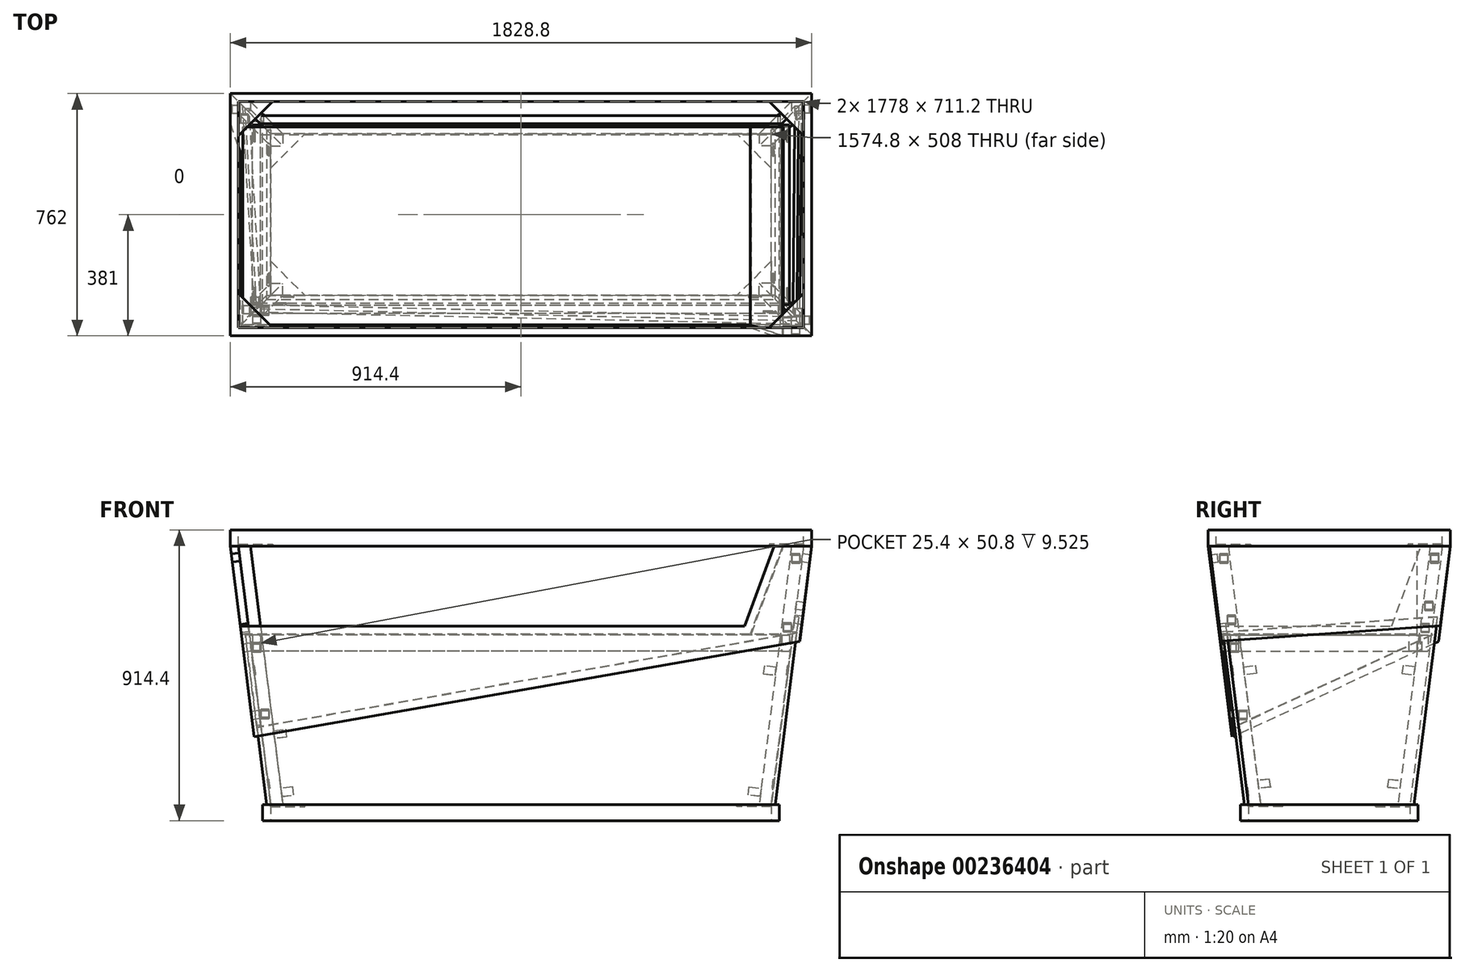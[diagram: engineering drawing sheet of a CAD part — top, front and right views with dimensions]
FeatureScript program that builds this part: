
annotation { "Feature Type Name" : "Feature", "Feature Type Description" : "" }
export const myFeature = defineFeature(function(context is Context, id is Id, definition is map)
    precondition{}
    {
        {
            var Q0;
            Q0=qCreatedBy(makeId("Top.planeOp"),FACE);
            cPlane(context, id + "F0", {"entities" : qUnion([Q0]), "cplaneType" : CPlaneType.OFFSET, "offset" : 914.4 * mm, "width" : 152.4 * mm, "height" : 152.4 * mm});
        }
        {
            var Q0;
            Q0=qCreatedBy(id+"F0.planeOp",FACE);
            var sketch = newSketch(context, id + "F1", { "sketchPlane" : qUnion([Q0])});
            skLineSegment(sketch, "E0.bottom", {"start": v(914.4, -381) * mm, "end": v(-914.4, -381) * mm});
            skLineSegment(sketch, "E0.top", {"start": v(914.4, 381) * mm, "end": v(-914.4, 381) * mm});
            skLineSegment(sketch, "E0.left", {"start": v(914.4, -381) * mm, "end": v(914.4, 381) * mm});
            skLineSegment(sketch, "E0.right", {"start": v(-914.4, -381) * mm, "end": v(-914.4, 381) * mm});
            skPoint(sketch, "E0.middle", {"position": v(0, 0) * mm});
            skLineSegment(sketch, "E1.0", {"start": v(889, 355.6) * mm, "end": v(-889, 355.6) * mm});
            skLineSegment(sketch, "E1.1", {"start": v(889, -355.6) * mm, "end": v(889, 355.6) * mm});
            skLineSegment(sketch, "E1.2", {"start": v(889, -355.6) * mm, "end": v(-889, -355.6) * mm});
            skLineSegment(sketch, "E1.3", {"start": v(-889, -355.6) * mm, "end": v(-889, 355.6) * mm});
            skSolve(sketch);
        }
        {
            var Q0;
            Q0 = qSketchRegion(id + "F1", true);
            extrude(context, id + "F2", {"entities" : qUnion([Q0]), "oppositeDirection" : true, "depth" : 50.8 * mm});
        }
        {
            var Q0;
            Q0=qCreatedBy(makeId("Top.planeOp"),FACE);
            var sketch = newSketch(context, id + "F3", { "sketchPlane" : qUnion([Q0])});
            skLineSegment(sketch, "E2.bottom", {"start": v(812.8, -279.4) * mm, "end": v(-812.8, -279.4) * mm});
            skLineSegment(sketch, "E2.top", {"start": v(812.8, 279.4) * mm, "end": v(-812.8, 279.4) * mm});
            skLineSegment(sketch, "E2.left", {"start": v(812.8, -279.4) * mm, "end": v(812.8, 279.4) * mm});
            skLineSegment(sketch, "E2.right", {"start": v(-812.8, -279.4) * mm, "end": v(-812.8, 279.4) * mm});
            skPoint(sketch, "E2.middle", {"position": v(0, 0) * mm});
            skLineSegment(sketch, "E3.0", {"start": v(787.4, 254) * mm, "end": v(-787.4, 254) * mm});
            skLineSegment(sketch, "E3.1", {"start": v(787.4, -254) * mm, "end": v(787.4, 254) * mm});
            skLineSegment(sketch, "E3.2", {"start": v(787.4, -254) * mm, "end": v(-787.4, -254) * mm});
            skLineSegment(sketch, "E3.3", {"start": v(-787.4, -254) * mm, "end": v(-787.4, 254) * mm});
            skSolve(sketch);
        }
        {
            var Q0;
            Q0 = qSketchRegion(id + "F3", true);
            extrude(context, id + "F4", {"entities" : qUnion([Q0]), "depth" : 50.8 * mm});
        }
        {
            var Q0;
            Q0=makeQuery(id+"F4.opExtrude","CAP_FACE",FACE,{"disambiguationData":[OSD([sQuery(id+"F3.wireOp",EDGE,"E2.bottom"),sQuery(id+"F3.wireOp",EDGE,"E2.top"),sQuery(id+"F3.wireOp",EDGE,"E2.left"),sQuery(id+"F3.wireOp",EDGE,"E2.right"),sQuery(id+"F3.wireOp",EDGE,"E3.0"),sQuery(id+"F3.wireOp",EDGE,"E3.1"),sQuery(id+"F3.wireOp",EDGE,"E3.2"),sQuery(id+"F3.wireOp",EDGE,"E3.3")])],"isStart":true});
            var sketch = newSketch(context, id + "F5", { "sketchPlane" : qUnion([Q0])});
            skLineSegment(sketch, "E4", {"start": v(-787.4, 496.92) * mm, "end": v(-787.4, -532.99) * mm, "construction": true});
            skLineSegment(sketch, "E5.MirrorCS", {"start": v(787.4, 496.92) * mm, "end": v(787.4, -532.99) * mm, "construction": true});
            skSolve(sketch);
        }
        {
            var Q0;
            Q0=makeQuery(id+"F2.opExtrude","CAP_FACE",FACE,{"disambiguationData":[OSD([sQuery(id+"F1.wireOp",EDGE,"E0.bottom"),sQuery(id+"F1.wireOp",EDGE,"E0.top"),sQuery(id+"F1.wireOp",EDGE,"E0.left"),sQuery(id+"F1.wireOp",EDGE,"E0.right"),sQuery(id+"F1.wireOp",EDGE,"E1.0"),sQuery(id+"F1.wireOp",EDGE,"E1.1"),sQuery(id+"F1.wireOp",EDGE,"E1.2"),sQuery(id+"F1.wireOp",EDGE,"E1.3")])],"isStart":false});
            var sketch = newSketch(context, id + "F6", { "sketchPlane" : qUnion([Q0])});
            skLineSegment(sketch, "E6", {"start": v(-889, 355.6) * mm, "end": v(-889, 247.84) * mm});
            skLineSegment(sketch, "E7", {"start": v(-889, 247.84) * mm, "end": v(-781.24, 355.6) * mm});
            skLineSegment(sketch, "E8", {"start": v(-781.24, 355.6) * mm, "end": v(-889, 355.6) * mm});
            skSolve(sketch);
        }
        {
            var Q0;
            Q0 = qSketchRegion(id + "F6", true);
            extrude(context, id + "F7", {"entities" : qUnion([Q0]), "oppositeDirection" : true, "depth" : 6.35 * mm});
        }
        {
            var Q0;
            Q0=makeQuery(id+"F7.opExtrude","SWEPT_BODY",BODY,{"disambiguationData":[OSD([sQuery(id+"F6.wireOp",EDGE,"E6"),sQuery(id+"F6.wireOp",EDGE,"E7"),sQuery(id+"F6.wireOp",EDGE,"E8")])]});
            var Q1;
            Q1=qCreatedBy(makeId("Front.planeOp"),FACE);
            mirror(context, id + "F8", {"entities" : qUnion([Q0]), "mirrorPlane" : qUnion([Q1])});
        }
        {
            var Q0;
            Q0=makeQuery(id+"F8.opPattern","COPY",BODY,{"derivedFrom":makeQuery(id+"F7.opExtrude","SWEPT_BODY",BODY,{"disambiguationData":[OSD([sQuery(id+"F6.wireOp",EDGE,"E6"),sQuery(id+"F6.wireOp",EDGE,"E7"),sQuery(id+"F6.wireOp",EDGE,"E8")])]}),"instanceName":"1"});
            var Q1;
            Q1=makeQuery(id+"F7.opExtrude","SWEPT_BODY",BODY,{"disambiguationData":[OSD([sQuery(id+"F6.wireOp",EDGE,"E6"),sQuery(id+"F6.wireOp",EDGE,"E7"),sQuery(id+"F6.wireOp",EDGE,"E8")])]});
            var Q2;
            Q2=qCreatedBy(makeId("Right.planeOp"),FACE);
            mirror(context, id + "F9", {"entities" : qUnion([Q0, Q1]), "mirrorPlane" : qUnion([Q2])});
        }
        {
            var Q0;
            Q0=makeQuery(id+"F4.opExtrude","CAP_FACE",FACE,{"disambiguationData":[OSD([sQuery(id+"F3.wireOp",EDGE,"E2.bottom"),sQuery(id+"F3.wireOp",EDGE,"E2.top"),sQuery(id+"F3.wireOp",EDGE,"E2.left"),sQuery(id+"F3.wireOp",EDGE,"E2.right"),sQuery(id+"F3.wireOp",EDGE,"E3.0"),sQuery(id+"F3.wireOp",EDGE,"E3.1"),sQuery(id+"F3.wireOp",EDGE,"E3.2"),sQuery(id+"F3.wireOp",EDGE,"E3.3")])],"isStart":false});
            var sketch = newSketch(context, id + "F10", { "sketchPlane" : qUnion([Q0])});
            skLineSegment(sketch, "E9", {"start": v(-787.4, 254) * mm, "end": v(-787.4, 146.24) * mm});
            skLineSegment(sketch, "E10", {"start": v(-787.4, 146.24) * mm, "end": v(-679.64, 254) * mm});
            skLineSegment(sketch, "E11", {"start": v(-679.64, 254) * mm, "end": v(-787.4, 254) * mm});
            skSolve(sketch);
        }
        {
            var Q0;
            Q0 = qSketchRegion(id + "F10", true);
            extrude(context, id + "F11", {"entities" : qUnion([Q0]), "oppositeDirection" : true, "depth" : 6.35 * mm});
        }
        {
            var Q0;
            Q0=makeQuery(id+"F11.opExtrude","SWEPT_BODY",BODY,{"disambiguationData":[OSD([sQuery(id+"F10.wireOp",EDGE,"E9"),sQuery(id+"F10.wireOp",EDGE,"E10"),sQuery(id+"F10.wireOp",EDGE,"E11")])]});
            var Q1;
            Q1=qCreatedBy(makeId("Right.planeOp"),FACE);
            mirror(context, id + "F12", {"entities" : qUnion([Q0]), "mirrorPlane" : qUnion([Q1])});
        }
        {
            var Q0;
            Q0=makeQuery(id+"F11.opExtrude","SWEPT_BODY",BODY,{"disambiguationData":[OSD([sQuery(id+"F10.wireOp",EDGE,"E9"),sQuery(id+"F10.wireOp",EDGE,"E10"),sQuery(id+"F10.wireOp",EDGE,"E11")])]});
            var Q1;
            Q1=makeQuery(id+"F12.opPattern","COPY",BODY,{"derivedFrom":makeQuery(id+"F11.opExtrude","SWEPT_BODY",BODY,{"disambiguationData":[OSD([sQuery(id+"F10.wireOp",EDGE,"E9"),sQuery(id+"F10.wireOp",EDGE,"E10"),sQuery(id+"F10.wireOp",EDGE,"E11")])]}),"instanceName":"1"});
            var Q2;
            Q2=qCreatedBy(makeId("Front.planeOp"),FACE);
            mirror(context, id + "F13", {"entities" : qUnion([Q0, Q1]), "mirrorPlane" : qUnion([Q2])});
        }
        {
            var Q0;
            Q0=makeQuery(id+"F11.opExtrude","CAP_FACE",FACE,{"disambiguationData":[OSD([sQuery(id+"F10.wireOp",EDGE,"E9"),sQuery(id+"F10.wireOp",EDGE,"E10"),sQuery(id+"F10.wireOp",EDGE,"E11")])],"isStart":true});
            var sketch = newSketch(context, id + "F14", { "sketchPlane" : qUnion([Q0])});
            skSolve(sketch);
        }
        {
            var Q0;
            Q0=makeQuery(id+"F14.imprint","IMPRINT",FACE,{"disambiguationData":[TD([[makeQuery(id+"F14.imprint","IMPRINT",EDGE,{"derivedFrom":makeQuery(id+"F11.opExtrude","CAP_EDGE",EDGE,{"disambiguationData":[OSD([sQuery(id+"F10.wireOp",EDGE,"E9")])],"isStart":true})}),-1.0]])]});
            var sketch = newSketch(context, id + "F15", { "sketchPlane" : qUnion([Q0])});
            skLineSegment(sketch, "E12.bottom", {"start": v(-787.4, 254) * mm, "end": v(-749.3, 254) * mm});
            skLineSegment(sketch, "E12.top", {"start": v(-787.4, 215.9) * mm, "end": v(-749.3, 215.9) * mm});
            skLineSegment(sketch, "E12.left", {"start": v(-787.4, 254) * mm, "end": v(-787.4, 215.9) * mm});
            skLineSegment(sketch, "E12.right", {"start": v(-749.3, 254) * mm, "end": v(-749.3, 215.9) * mm});
            skSolve(sketch);
        }
        {
            var Q0;
            Q0=makeQuery(id+"F8.opPattern","COPY",FACE,{"derivedFrom":makeQuery(id+"F7.opExtrude","CAP_FACE",FACE,{"disambiguationData":[OSD([sQuery(id+"F6.wireOp",EDGE,"E6"),sQuery(id+"F6.wireOp",EDGE,"E7"),sQuery(id+"F6.wireOp",EDGE,"E8")])],"isStart":true}),"instanceName":"1"});
            var sketch = newSketch(context, id + "F16", { "sketchPlane" : qUnion([Q0])});
            skLineSegment(sketch, "E13.bottom", {"start": v(-889, -355.6) * mm, "end": v(-850.9, -355.6) * mm});
            skLineSegment(sketch, "E13.top", {"start": v(-889, -317.5) * mm, "end": v(-850.9, -317.5) * mm});
            skLineSegment(sketch, "E13.left", {"start": v(-889, -355.6) * mm, "end": v(-889, -317.5) * mm});
            skLineSegment(sketch, "E13.right", {"start": v(-850.9, -355.6) * mm, "end": v(-850.9, -317.5) * mm});
            skSolve(sketch);
        }
        {
            var Q0;
            Q0=makeQuery(id+"F16.imprint","IMPRINT",FACE,{"disambiguationData":[TD([[makeQuery(id+"F16.imprint","IMPRINT",EDGE,{"derivedFrom":sQuery(id+"F16.wireOp",EDGE,"E13.bottom")}),-1.0]])]});
            var Q1;
            Q1=makeQuery(id+"F15.imprint","IMPRINT",FACE,{"disambiguationData":[TD([[makeQuery(id+"F15.imprint","IMPRINT",EDGE,{"derivedFrom":sQuery(id+"F15.wireOp",EDGE,"E12.bottom")}),1.0]])]});
            loft(context, id + "F17", {"sheetProfilesArray" : [{ "sheetProfileEntities" : qUnion([Q0]) }, { "sheetProfileEntities" : qUnion([Q1]) }]});
        }
        {
            var Q0;
            Q0=makeQuery(id+"F17.opLoft","SWEPT_BODY",BODY,{"disambiguationData":[OSD([makeQuery(id+"F15.imprint","IMPRINT",FACE,{"disambiguationData":[TD([[makeQuery(id+"F15.imprint","IMPRINT",EDGE,{"derivedFrom":sQuery(id+"F15.wireOp",EDGE,"E12.bottom")}),1.0]])]}),makeQuery(id+"F16.imprint","IMPRINT",FACE,{"disambiguationData":[TD([[makeQuery(id+"F16.imprint","IMPRINT",EDGE,{"derivedFrom":sQuery(id+"F16.wireOp",EDGE,"E13.bottom")}),-1.0]])]})])]});
            var Q1;
            Q1=qCreatedBy(makeId("Front.planeOp"),FACE);
            mirror(context, id + "F18", {"entities" : qUnion([Q0]), "mirrorPlane" : qUnion([Q1])});
        }
        {
            var Q0;
            Q0=makeQuery(id+"F17.opLoft","SWEPT_BODY",BODY,{"disambiguationData":[OSD([makeQuery(id+"F15.imprint","IMPRINT",FACE,{"disambiguationData":[TD([[makeQuery(id+"F15.imprint","IMPRINT",EDGE,{"derivedFrom":sQuery(id+"F15.wireOp",EDGE,"E12.bottom")}),1.0]])]}),makeQuery(id+"F16.imprint","IMPRINT",FACE,{"disambiguationData":[TD([[makeQuery(id+"F16.imprint","IMPRINT",EDGE,{"derivedFrom":sQuery(id+"F16.wireOp",EDGE,"E13.bottom")}),-1.0]])]})])]});
            var Q1;
            Q1=makeQuery(id+"F18.opPattern","COPY",BODY,{"derivedFrom":makeQuery(id+"F17.opLoft","SWEPT_BODY",BODY,{"disambiguationData":[OSD([makeQuery(id+"F15.imprint","IMPRINT",FACE,{"disambiguationData":[TD([[makeQuery(id+"F15.imprint","IMPRINT",EDGE,{"derivedFrom":sQuery(id+"F15.wireOp",EDGE,"E12.bottom")}),1.0]])]}),makeQuery(id+"F16.imprint","IMPRINT",FACE,{"disambiguationData":[TD([[makeQuery(id+"F16.imprint","IMPRINT",EDGE,{"derivedFrom":sQuery(id+"F16.wireOp",EDGE,"E13.bottom")}),-1.0]])]})])]}),"instanceName":"1"});
            var Q2;
            Q2=qCreatedBy(makeId("Right.planeOp"),FACE);
            mirror(context, id + "F19", {"entities" : qUnion([Q0, Q1]), "mirrorPlane" : qUnion([Q2])});
        }
        {
            var Q0;
            Q0=makeQuery(id+"F2.opExtrude","CAP_VERTEX",VERTEX,{"disambiguationData":[OSD([sQuery(id+"F1.wireOp",EDGE,"E0.bottom"),sQuery(id+"F1.wireOp",EDGE,"E0.right")])],"isStart":false});
            var Q1;
            Q1=makeQuery(id+"F4.opExtrude","CAP_VERTEX",VERTEX,{"disambiguationData":[OSD([sQuery(id+"F3.wireOp",EDGE,"E2.bottom"),sQuery(id+"F3.wireOp",EDGE,"E2.right")])],"isStart":false});
            var Q2;
            Q2=makeQuery(id+"F4.opExtrude","CAP_VERTEX",VERTEX,{"disambiguationData":[OSD([sQuery(id+"F3.wireOp",EDGE,"E2.bottom"),sQuery(id+"F3.wireOp",EDGE,"E2.left")])],"isStart":false});
            cPlane(context, id + "F20", {"entities" : qUnion([Q0, Q1, Q2]), "cplaneType" : CPlaneType.THREE_POINT, "offset" : 25.4 * mm, "width" : 152.4 * mm, "height" : 152.4 * mm});
        }
        {
            var Q0;
            Q0=qCreatedBy(id+"F20.planeOp",FACE);
            var sketch = newSketch(context, id + "F21", { "sketchPlane" : qUnion([Q0])});
            skLineSegment(sketch, "E14", {"start": v(882.9, 650.19) * mm, "end": v(839.36, 299.22) * mm});
            skLineSegment(sketch, "E15", {"start": v(839.36, 299.22) * mm, "end": v(-876.88, 601.7) * mm});
            skLineSegment(sketch, "E16", {"start": v(-876.88, 601.7) * mm, "end": v(-914.4, 904.19) * mm});
            skLineSegment(sketch, "E17", {"start": v(-914.4, 904.19) * mm, "end": v(-796.58, 904.19) * mm});
            skLineSegment(sketch, "E18", {"start": v(882.9, 650.19) * mm, "end": v(-704.13, 650.19) * mm});
            skLineSegment(sketch, "E19", {"start": v(-704.13, 650.19) * mm, "end": v(-796.58, 904.19) * mm});
            skSolve(sketch);
        }
        {
            var Q0;
            Q0 = qSketchRegion(id + "F21", true);
            extrude(context, id + "F22", {"entities" : qUnion([Q0]), "depth" : 3 / 406.4 * mm});
        }
        {
            var Q0;
            Q0=makeQuery(id+"F2.opExtrude","CAP_VERTEX",VERTEX,{"disambiguationData":[OSD([sQuery(id+"F1.wireOp",EDGE,"E0.bottom"),sQuery(id+"F1.wireOp",EDGE,"E0.right")])],"isStart":false});
            var Q1;
            Q1=makeQuery(id+"F4.opExtrude","CAP_VERTEX",VERTEX,{"disambiguationData":[OSD([sQuery(id+"F3.wireOp",EDGE,"E2.bottom"),sQuery(id+"F3.wireOp",EDGE,"E2.right")])],"isStart":false});
            var Q2;
            Q2=makeQuery(id+"F4.opExtrude","CAP_VERTEX",VERTEX,{"disambiguationData":[OSD([sQuery(id+"F3.wireOp",EDGE,"E2.top"),sQuery(id+"F3.wireOp",EDGE,"E2.right")])],"isStart":false});
            cPlane(context, id + "F23", {"entities" : qUnion([Q0, Q1, Q2]), "cplaneType" : CPlaneType.THREE_POINT, "offset" : 25.4 * mm, "width" : 152.4 * mm, "height" : 152.4 * mm});
        }
        {
            var Q0;
            Q0=qCreatedBy(id+"F23.planeOp",FACE);
            var sketch = newSketch(context, id + "F24", { "sketchPlane" : qUnion([Q0])});
            skLineSegment(sketch, "E20", {"start": v(-381, 970.35) * mm, "end": v(-343.48, 667.87) * mm});
            skLineSegment(sketch, "E21", {"start": v(-343.48, 667.87) * mm, "end": v(301.24, 365.97) * mm});
            skLineSegment(sketch, "E22", {"start": v(301.24, 365.97) * mm, "end": v(344.7, 716.35) * mm});
            skLineSegment(sketch, "E23", {"start": v(-289.03, 970.35) * mm, "end": v(-381, 970.35) * mm});
            skLineSegment(sketch, "E24", {"start": v(344.7, 716.35) * mm, "end": v(-196.59, 716.35) * mm});
            skLineSegment(sketch, "E25", {"start": v(-196.59, 716.35) * mm, "end": v(-289.03, 970.35) * mm});
            skSolve(sketch);
        }
        {
            var Q0;
            Q0 = qSketchRegion(id + "F24", true);
            extrude(context, id + "F25", {"entities" : qUnion([Q0]), "oppositeDirection" : true, "depth" : 3 / 406.4 * mm});
        }
        {
            var Q0;
            Q0=sQuery(id+"F21.wireOp",VERTEX,"E17.start");
            var Q1;
            Q1=makeQuery(id+"F4.opExtrude","CAP_VERTEX",VERTEX,{"disambiguationData":[OSD([sQuery(id+"F3.wireOp",EDGE,"E2.bottom"),sQuery(id+"F3.wireOp",EDGE,"E2.left")])],"isStart":false});
            var Q2;
            Q2=makeQuery(id+"F2.opExtrude","CAP_VERTEX",VERTEX,{"disambiguationData":[OSD([sQuery(id+"F1.wireOp",EDGE,"E0.top"),sQuery(id+"F1.wireOp",EDGE,"E0.left")])],"isStart":false});
            cPlane(context, id + "F26", {"entities" : qUnion([Q0, Q1, Q2]), "cplaneType" : CPlaneType.THREE_POINT, "offset" : 25.4 * mm, "width" : 152.4 * mm, "height" : 152.4 * mm});
        }
        {
            var Q0;
            Q0=qCreatedBy(id+"F26.planeOp",FACE);
            var sketch = newSketch(context, id + "F27", { "sketchPlane" : qUnion([Q0])});
            skLineSegment(sketch, "E26", {"start": v(376.2, 970.35) * mm, "end": v(338.76, 668.45) * mm});
            skLineSegment(sketch, "E27", {"start": v(338.76, 668.45) * mm, "end": v(-349.73, 718.28) * mm});
            skLineSegment(sketch, "E28", {"start": v(-349.73, 718.28) * mm, "end": v(-381, 970.35) * mm});
            skLineSegment(sketch, "E29", {"start": v(-381, 970.35) * mm, "end": v(376.2, 970.35) * mm});
            skSolve(sketch);
        }
        {
            var Q0;
            Q0 = qSketchRegion(id + "F27", true);
            extrude(context, id + "F28", {"entities" : qUnion([Q0]), "depth" : 3 / 406.4 * mm});
        }
        {
            var Q0;
            Q0=makeQuery(id+"F2.opExtrude","SWEPT_FACE",FACE,{"disambiguationData":[OSD([sQuery(id+"F1.wireOp",EDGE,"E0.bottom")])]});
            var sketch = newSketch(context, id + "F29", { "sketchPlane" : qUnion([Q0])});
            skLineSegment(sketch, "E30", {"start": v(-889, 863.6) * mm, "end": v(-850.9, 863.6) * mm});
            skLineSegment(sketch, "E31", {"start": v(-850.9, 863.6) * mm, "end": v(-815.98, 584.2) * mm});
            skLineSegment(sketch, "E32", {"start": v(-815.98, 584.2) * mm, "end": v(-854.08, 584.2) * mm});
            skLineSegment(sketch, "E33", {"start": v(-854.08, 584.2) * mm, "end": v(-889, 863.6) * mm});
            skSolve(sketch);
        }
        {
            var Q0;
            Q0=makeQuery(id+"F18.opPattern","COPY",FACE,{"derivedFrom":makeQuery(id+"F17.opLoft","SWEPT_FACE",FACE,{"disambiguationData":[OSD([sQuery(id+"F6.wireOp",EDGE,"E8"),sQuery(id+"F10.wireOp",EDGE,"E11"),sQuery(id+"F15.wireOp",EDGE,"E12.bottom"),sQuery(id+"F15.wireOp",EDGE,"E12.left"),sQuery(id+"F15.wireOp",EDGE,"E12.right"),sQuery(id+"F16.wireOp",EDGE,"E13.bottom"),sQuery(id+"F16.wireOp",EDGE,"E13.left"),sQuery(id+"F16.wireOp",EDGE,"E13.right")])]}),"instanceName":"1"});
            var sketch = newSketch(context, id + "F30", { "sketchPlane" : qUnion([Q0])});
            skLineSegment(sketch, "E34", {"start": v(-830.54, 326.57) * mm, "end": v(-800.2, 81.91) * mm});
            skLineSegment(sketch, "E35", {"start": v(-800.2, 81.91) * mm, "end": v(800.2, 81.91) * mm});
            skLineSegment(sketch, "E36", {"start": v(800.2, 81.91) * mm, "end": v(867.67, 625.87) * mm});
            skLineSegment(sketch, "E37", {"start": v(867.67, 625.87) * mm, "end": v(-830.54, 326.57) * mm});
            skSolve(sketch);
        }
        {
            var Q0;
            Q0 = qSketchRegion(id + "F30", true);
            extrude(context, id + "F31", {"entities" : qUnion([Q0]), "depth" : 12.7 * mm});
        }
        {
            var Q0;
            Q0=makeQuery(id+"F18.opPattern","COPY",FACE,{"derivedFrom":makeQuery(id+"F17.opLoft","SWEPT_FACE",FACE,{"disambiguationData":[OSD([sQuery(id+"F6.wireOp",EDGE,"E6"),sQuery(id+"F10.wireOp",EDGE,"E9"),sQuery(id+"F15.wireOp",EDGE,"E12.bottom"),sQuery(id+"F15.wireOp",EDGE,"E12.top"),sQuery(id+"F15.wireOp",EDGE,"E12.left"),sQuery(id+"F16.wireOp",EDGE,"E13.bottom"),sQuery(id+"F16.wireOp",EDGE,"E13.top"),sQuery(id+"F16.wireOp",EDGE,"E13.left")])]}),"instanceName":"1"});
            var sketch = newSketch(context, id + "F32", { "sketchPlane" : qUnion([Q0])});
            skLineSegment(sketch, "E38", {"start": v(-334.21, 691.57) * mm, "end": v(-266.8, 148.07) * mm});
            skLineSegment(sketch, "E39", {"start": v(-266.8, 148.07) * mm, "end": v(254, 148.07) * mm});
            skLineSegment(sketch, "E40", {"start": v(254, 148.07) * mm, "end": v(285.42, 401.42) * mm});
            skLineSegment(sketch, "E41", {"start": v(285.42, 401.42) * mm, "end": v(-334.21, 691.57) * mm});
            skSolve(sketch);
        }
        {
            var Q0;
            Q0 = qSketchRegion(id + "F32", true);
            extrude(context, id + "F33", {"entities" : qUnion([Q0]), "depth" : 12.7 * mm});
        }
        {
            var Q0;
            Q0=makeQuery(id+"F19.opPattern","COPY",FACE,{"derivedFrom":makeQuery(id+"F18.opPattern","COPY",FACE,{"derivedFrom":makeQuery(id+"F17.opLoft","SWEPT_FACE",FACE,{"disambiguationData":[OSD([sQuery(id+"F6.wireOp",EDGE,"E6"),sQuery(id+"F10.wireOp",EDGE,"E9"),sQuery(id+"F15.wireOp",EDGE,"E12.bottom"),sQuery(id+"F15.wireOp",EDGE,"E12.top"),sQuery(id+"F15.wireOp",EDGE,"E12.left"),sQuery(id+"F16.wireOp",EDGE,"E13.bottom"),sQuery(id+"F16.wireOp",EDGE,"E13.top"),sQuery(id+"F16.wireOp",EDGE,"E13.left")])]}),"instanceName":"1"}),"instanceName":"1"});
            var sketch = newSketch(context, id + "F34", { "sketchPlane" : qUnion([Q0])});
            skLineSegment(sketch, "E42", {"start": v(-321.86, 695.14) * mm, "end": v(-254, 148.07) * mm});
            skLineSegment(sketch, "E43", {"start": v(-254, 148.07) * mm, "end": v(266.8, 148.07) * mm});
            skLineSegment(sketch, "E44", {"start": v(266.8, 148.07) * mm, "end": v(340.6, 743.09) * mm});
            skLineSegment(sketch, "E45", {"start": v(340.6, 743.09) * mm, "end": v(-321.86, 695.14) * mm});
            skSolve(sketch);
        }
        {
            var Q0;
            Q0 = qSketchRegion(id + "F34", true);
            extrude(context, id + "F35", {"entities" : qUnion([Q0]), "depth" : 12.7 * mm});
        }
        {
            var Q0;
            Q0=makeQuery(id+"F2.opExtrude","SWEPT_FACE",FACE,{"disambiguationData":[OSD([sQuery(id+"F1.wireOp",EDGE,"E0.bottom")])]});
            var sketch = newSketch(context, id + "F36", { "sketchPlane" : qUnion([Q0])});
            skLineSegment(sketch, "E46", {"start": v(-889, 863.6) * mm, "end": v(-854.08, 584.2) * mm});
            skLineSegment(sketch, "E47", {"start": v(-854.08, 584.2) * mm, "end": v(-815.98, 584.2) * mm});
            skLineSegment(sketch, "E48", {"start": v(-815.98, 584.2) * mm, "end": v(-850.9, 863.6) * mm});
            skLineSegment(sketch, "E49", {"start": v(-850.9, 863.6) * mm, "end": v(-889, 863.6) * mm});
            skSolve(sketch);
        }
        {
            var Q0;
            Q0 = qSketchRegion(id + "F36", true);
            extrude(context, id + "F37", {"entities" : qUnion([Q0]), "operationType" : NewBodyOperationType.REMOVE, "oppositeDirection" : true, "depth" : 116.08 * mm});
        }
        {
            var Q0;
            Q0=makeQuery(id+"F18.opPattern","COPY",FACE,{"derivedFrom":makeQuery(id+"F17.opLoft","SWEPT_FACE",FACE,{"disambiguationData":[OSD([sQuery(id+"F6.wireOp",EDGE,"E8"),sQuery(id+"F10.wireOp",EDGE,"E11"),sQuery(id+"F15.wireOp",EDGE,"E12.bottom"),sQuery(id+"F15.wireOp",EDGE,"E12.top"),sQuery(id+"F15.wireOp",EDGE,"E12.right"),sQuery(id+"F16.wireOp",EDGE,"E13.bottom"),sQuery(id+"F16.wireOp",EDGE,"E13.top"),sQuery(id+"F16.wireOp",EDGE,"E13.right")])]}),"instanceName":"1"});
            var sketch = newSketch(context, id + "F38", { "sketchPlane" : qUnion([Q0])});
            skLineSegment(sketch, "E50", {"start": v(-301.62, 680.9) * mm, "end": v(-234.95, 143.35) * mm, "construction": true});
            skSolve(sketch);
        }
        {
            var Q0;
            Q0=qCreatedBy(makeId("Right.planeOp"),FACE);
            var sketch = newSketch(context, id + "F39", { "sketchPlane" : qUnion([Q0])});
            skLineSegment(sketch, "E51.bottom", {"start": v(-285.75, 533.4) * mm, "end": v(-311.15, 533.4) * mm});
            skLineSegment(sketch, "E51.top", {"start": v(-285.75, 584.2) * mm, "end": v(-311.15, 584.2) * mm});
            skLineSegment(sketch, "E51.left", {"start": v(-285.75, 533.4) * mm, "end": v(-285.75, 584.2) * mm});
            skLineSegment(sketch, "E51.right", {"start": v(-311.15, 533.4) * mm, "end": v(-311.15, 584.2) * mm});
            skPoint(sketch, "E51.middle", {"position": v(-298.45, 558.8) * mm});
            skSolve(sketch);
        }
        {
            var Q0;
            Q0 = qSketchRegion(id + "F39", true);
            extrude(context, id + "F40", {"entities" : qUnion([Q0]), "depth" : 819.9 * mm, "hasSecondDirection" : true, "secondDirectionOppositeDirection" : true, "secondDirectionDepth" : 819.9 * mm});
        }
        {
            var Q0;
            Q0=makeQuery(id+"F40.opExtrude","SWEPT_FACE",FACE,{"disambiguationData":[OSD([sQuery(id+"F39.wireOp",EDGE,"E51.right")])]});
            var sketch = newSketch(context, id + "F41", { "sketchPlane" : qUnion([Q0])});
            skLineSegment(sketch, "E52", {"start": v(-815.98, 584.2) * mm, "end": v(-809.62, 533.4) * mm});
            skLineSegment(sketch, "E53", {"start": v(-815.98, 584.2) * mm, "end": v(-819.91, 584.2) * mm});
            skLineSegment(sketch, "E54", {"start": v(-819.91, 584.2) * mm, "end": v(-819.91, 533.4) * mm});
            skLineSegment(sketch, "E55", {"start": v(-819.91, 533.4) * mm, "end": v(-809.62, 533.4) * mm});
            skLineSegment(sketch, "E56.MirrorCS", {"start": v(819.91, 584.2) * mm, "end": v(819.91, 533.4) * mm});
            skLineSegment(sketch, "E57.MirrorCS", {"start": v(815.98, 584.2) * mm, "end": v(809.62, 533.4) * mm});
            skLineSegment(sketch, "E58.MirrorCS", {"start": v(819.91, 533.4) * mm, "end": v(809.62, 533.4) * mm});
            skLineSegment(sketch, "E59.MirrorCS", {"start": v(815.98, 584.2) * mm, "end": v(819.91, 584.2) * mm});
            skSolve(sketch);
        }
        {
            var Q0;
            Q0 = qSketchRegion(id + "F41", true);
            extrude(context, id + "F42", {"entities" : qUnion([Q0]), "operationType" : NewBodyOperationType.REMOVE, "oppositeDirection" : true, "depth" : 25.4 * mm});
        }
        {
            var Q0;
            Q0=makeQuery(id+"F40.opExtrude","SWEPT_BODY",BODY,{"disambiguationData":[OSD([sQuery(id+"F39.wireOp",EDGE,"E51.bottom"),sQuery(id+"F39.wireOp",EDGE,"E51.top"),sQuery(id+"F39.wireOp",EDGE,"E51.left"),sQuery(id+"F39.wireOp",EDGE,"E51.right")])]});
            var Q1;
            Q1=qCreatedBy(makeId("Front.planeOp"),FACE);
            mirror(context, id + "F43", {"entities" : qUnion([Q0]), "mirrorPlane" : qUnion([Q1])});
        }
        {
            var Q0;
            Q0=makeQuery(id+"F18.opPattern","COPY",FACE,{"derivedFrom":makeQuery(id+"F17.opLoft","SWEPT_FACE",FACE,{"disambiguationData":[OSD([sQuery(id+"F6.wireOp",EDGE,"E6"),sQuery(id+"F10.wireOp",EDGE,"E9"),sQuery(id+"F15.wireOp",EDGE,"E12.top"),sQuery(id+"F15.wireOp",EDGE,"E12.left"),sQuery(id+"F15.wireOp",EDGE,"E12.right"),sQuery(id+"F16.wireOp",EDGE,"E13.top"),sQuery(id+"F16.wireOp",EDGE,"E13.left"),sQuery(id+"F16.wireOp",EDGE,"E13.right")])]}),"instanceName":"1"});
            var sketch = newSketch(context, id + "F44", { "sketchPlane" : qUnion([Q0])});
            skLineSegment(sketch, "E60", {"start": v(835.02, 614.74) * mm, "end": v(768.35, 77.19) * mm, "construction": true});
            skSolve(sketch);
        }
        {
            var Q0;
            Q0=qCreatedBy(makeId("Front.planeOp"),FACE);
            var sketch = newSketch(context, id + "F45", { "sketchPlane" : qUnion([Q0])});
            skLineSegment(sketch, "E61.bottom", {"start": v(-844.55, 533.4) * mm, "end": v(-819.15, 533.4) * mm});
            skLineSegment(sketch, "E61.top", {"start": v(-844.55, 584.2) * mm, "end": v(-819.15, 584.2) * mm});
            skLineSegment(sketch, "E61.left", {"start": v(-844.55, 533.4) * mm, "end": v(-844.55, 584.2) * mm});
            skLineSegment(sketch, "E61.right", {"start": v(-819.15, 533.4) * mm, "end": v(-819.15, 584.2) * mm});
            skPoint(sketch, "E61.middle", {"position": v(-831.85, 558.8) * mm});
            skSolve(sketch);
        }
        {
            var Q0;
            Q0 = qSketchRegion(id + "F45", true);
            extrude(context, id + "F46", {"entities" : qUnion([Q0]), "depth" : 292.1 * mm, "hasSecondDirection" : true, "secondDirectionOppositeDirection" : true, "secondDirectionDepth" : 292.1 * mm});
        }
        {
            var Q0;
            Q0=makeQuery(id+"F46.opExtrude","SWEPT_FACE",FACE,{"disambiguationData":[OSD([sQuery(id+"F45.wireOp",EDGE,"E61.left")])]});
            var sketch = newSketch(context, id + "F47", { "sketchPlane" : qUnion([Q0])});
            skLineSegment(sketch, "E62", {"start": v(282.57, 584.2) * mm, "end": v(276.22, 533.4) * mm});
            skLineSegment(sketch, "E63", {"start": v(282.57, 584.2) * mm, "end": v(292.1, 584.2) * mm});
            skLineSegment(sketch, "E64", {"start": v(292.1, 584.2) * mm, "end": v(292.1, 533.4) * mm});
            skLineSegment(sketch, "E65", {"start": v(292.1, 533.4) * mm, "end": v(276.22, 533.4) * mm});
            skLineSegment(sketch, "E66.MirrorCS", {"start": v(-282.57, 584.2) * mm, "end": v(-276.22, 533.4) * mm});
            skLineSegment(sketch, "E67.MirrorCS", {"start": v(-292.1, 584.2) * mm, "end": v(-292.1, 533.4) * mm});
            skLineSegment(sketch, "E68.MirrorCS", {"start": v(-282.57, 584.2) * mm, "end": v(-292.1, 584.2) * mm});
            skLineSegment(sketch, "E69.MirrorCS", {"start": v(-292.1, 533.4) * mm, "end": v(-276.22, 533.4) * mm});
            skSolve(sketch);
        }
        {
            var Q0;
            Q0 = qSketchRegion(id + "F47", true);
            extrude(context, id + "F48", {"entities" : qUnion([Q0]), "operationType" : NewBodyOperationType.REMOVE, "oppositeDirection" : true, "depth" : 25.4 * mm});
        }
        {
            var Q0;
            Q0=makeQuery(id+"F46.opExtrude","SWEPT_BODY",BODY,{"disambiguationData":[OSD([sQuery(id+"F45.wireOp",EDGE,"E61.bottom"),sQuery(id+"F45.wireOp",EDGE,"E61.top"),sQuery(id+"F45.wireOp",EDGE,"E61.left"),sQuery(id+"F45.wireOp",EDGE,"E61.right")])]});
            var Q1;
            Q1=qCreatedBy(makeId("Right.planeOp"),FACE);
            mirror(context, id + "F49", {"entities" : qUnion([Q0]), "mirrorPlane" : qUnion([Q1])});
        }
        {
            var Q0;
            Q0=makeQuery(id+"F19.opPattern","COPY",FACE,{"derivedFrom":makeQuery(id+"F17.opLoft","SWEPT_FACE",FACE,{"disambiguationData":[OSD([sQuery(id+"F6.wireOp",EDGE,"E6"),sQuery(id+"F10.wireOp",EDGE,"E9"),sQuery(id+"F15.wireOp",EDGE,"E12.bottom"),sQuery(id+"F15.wireOp",EDGE,"E12.top"),sQuery(id+"F15.wireOp",EDGE,"E12.left"),sQuery(id+"F16.wireOp",EDGE,"E13.bottom"),sQuery(id+"F16.wireOp",EDGE,"E13.top"),sQuery(id+"F16.wireOp",EDGE,"E13.left")])]}),"instanceName":"1"});
            var sketch = newSketch(context, id + "F50", { "sketchPlane" : qUnion([Q0])});
            skLineSegment(sketch, "E70", {"start": v(184.34, 203.18) * mm, "end": v(187.47, 228.38) * mm});
            skLineSegment(sketch, "E71", {"start": v(184.34, 203.18) * mm, "end": v(222.15, 198.49) * mm});
            skLineSegment(sketch, "E72", {"start": v(187.47, 228.38) * mm, "end": v(225.28, 223.7) * mm});
            skLineSegment(sketch, "E73", {"start": v(225.28, 223.7) * mm, "end": v(222.15, 198.49) * mm});
            skPoint(sketch, "E74.centerSnap0", {"position": v(185.9, 215.78) * mm});
            skSolve(sketch);
        }
        {
            var Q0;
            Q0 = qSketchRegion(id + "F50", true);
            extrude(context, id + "F51", {"entities" : qUnion([Q0]), "oppositeDirection" : true, "depth" : 3.17 * mm});
        }
        {
            var Q0;
            Q0=makeQuery(id+"F19.opPattern","COPY",FACE,{"derivedFrom":makeQuery(id+"F17.opLoft","SWEPT_FACE",FACE,{"disambiguationData":[OSD([sQuery(id+"F6.wireOp",EDGE,"E6"),sQuery(id+"F10.wireOp",EDGE,"E9"),sQuery(id+"F15.wireOp",EDGE,"E12.bottom"),sQuery(id+"F15.wireOp",EDGE,"E12.top"),sQuery(id+"F15.wireOp",EDGE,"E12.left"),sQuery(id+"F16.wireOp",EDGE,"E13.bottom"),sQuery(id+"F16.wireOp",EDGE,"E13.top"),sQuery(id+"F16.wireOp",EDGE,"E13.left")])]}),"instanceName":"1"});
            var sketch = newSketch(context, id + "F52", { "sketchPlane" : qUnion([Q0])});
            skLineSegment(sketch, "E75", {"start": v(269.92, 583.63) * mm, "end": v(232.11, 588.32) * mm});
            skLineSegment(sketch, "E76", {"start": v(232.11, 588.32) * mm, "end": v(228.99, 563.1) * mm});
            skLineSegment(sketch, "E77", {"start": v(228.99, 563.1) * mm, "end": v(266.8, 558.42) * mm});
            skLineSegment(sketch, "E78", {"start": v(266.8, 558.42) * mm, "end": v(269.92, 583.63) * mm});
            skSolve(sketch);
        }
        {
            var Q0;
            Q0 = qSketchRegion(id + "F52", true);
            extrude(context, id + "F53", {"entities" : qUnion([Q0]), "oppositeDirection" : true, "depth" : 3.17 * mm});
        }
        {
            var Q0;
            Q0=makeQuery(id+"F53.opExtrude","SWEPT_BODY",BODY,{"disambiguationData":[OSD([sQuery(id+"F52.wireOp",EDGE,"E75"),sQuery(id+"F52.wireOp",EDGE,"E76"),sQuery(id+"F52.wireOp",EDGE,"E77"),sQuery(id+"F52.wireOp",EDGE,"E78")])]});
            var Q1;
            Q1=makeQuery(id+"F51.opExtrude","SWEPT_BODY",BODY,{"disambiguationData":[OSD([sQuery(id+"F50.wireOp",EDGE,"E70"),sQuery(id+"F50.wireOp",EDGE,"E71"),sQuery(id+"F50.wireOp",EDGE,"E72"),sQuery(id+"F50.wireOp",EDGE,"E73")])]});
            var Q2;
            Q2=qCreatedBy(makeId("Front.planeOp"),FACE);
            mirror(context, id + "F54", {"entities" : qUnion([Q0, Q1]), "mirrorPlane" : qUnion([Q2])});
        }
        {
            var Q0;
            Q0=makeQuery(id+"F54.opPattern","COPY",BODY,{"derivedFrom":makeQuery(id+"F53.opExtrude","SWEPT_BODY",BODY,{"disambiguationData":[OSD([sQuery(id+"F52.wireOp",EDGE,"E75"),sQuery(id+"F52.wireOp",EDGE,"E76"),sQuery(id+"F52.wireOp",EDGE,"E77"),sQuery(id+"F52.wireOp",EDGE,"E78")])]}),"instanceName":"1"});
            var Q1;
            Q1=makeQuery(id+"F53.opExtrude","SWEPT_BODY",BODY,{"disambiguationData":[OSD([sQuery(id+"F52.wireOp",EDGE,"E75"),sQuery(id+"F52.wireOp",EDGE,"E76"),sQuery(id+"F52.wireOp",EDGE,"E77"),sQuery(id+"F52.wireOp",EDGE,"E78")])]});
            var Q2;
            Q2=makeQuery(id+"F51.opExtrude","SWEPT_BODY",BODY,{"disambiguationData":[OSD([sQuery(id+"F50.wireOp",EDGE,"E70"),sQuery(id+"F50.wireOp",EDGE,"E71"),sQuery(id+"F50.wireOp",EDGE,"E72"),sQuery(id+"F50.wireOp",EDGE,"E73")])]});
            var Q3;
            Q3=makeQuery(id+"F54.opPattern","COPY",BODY,{"derivedFrom":makeQuery(id+"F51.opExtrude","SWEPT_BODY",BODY,{"disambiguationData":[OSD([sQuery(id+"F50.wireOp",EDGE,"E70"),sQuery(id+"F50.wireOp",EDGE,"E71"),sQuery(id+"F50.wireOp",EDGE,"E72"),sQuery(id+"F50.wireOp",EDGE,"E73")])]}),"instanceName":"1"});
            var Q4;
            Q4=qCreatedBy(makeId("Right.planeOp"),FACE);
            mirror(context, id + "F55", {"entities" : qUnion([Q0, Q1, Q2, Q3]), "mirrorPlane" : qUnion([Q4])});
        }
        {
            var Q0;
            Q0=makeQuery(id+"F18.opPattern","COPY",FACE,{"derivedFrom":makeQuery(id+"F17.opLoft","SWEPT_FACE",FACE,{"disambiguationData":[OSD([sQuery(id+"F6.wireOp",EDGE,"E8"),sQuery(id+"F10.wireOp",EDGE,"E11"),sQuery(id+"F15.wireOp",EDGE,"E12.bottom"),sQuery(id+"F15.wireOp",EDGE,"E12.left"),sQuery(id+"F15.wireOp",EDGE,"E12.right"),sQuery(id+"F16.wireOp",EDGE,"E13.bottom"),sQuery(id+"F16.wireOp",EDGE,"E13.left"),sQuery(id+"F16.wireOp",EDGE,"E13.right")])]}),"instanceName":"1"});
            var sketch = newSketch(context, id + "F56", { "sketchPlane" : qUnion([Q0])});
            skLineSegment(sketch, "E79", {"start": v(-778.3, 315.76) * mm, "end": v(-740.5, 320.45) * mm});
            skLineSegment(sketch, "E80", {"start": v(-740.5, 320.45) * mm, "end": v(-737.37, 295.24) * mm});
            skLineSegment(sketch, "E81", {"start": v(-737.37, 295.24) * mm, "end": v(-775.18, 290.55) * mm});
            skLineSegment(sketch, "E82", {"start": v(-775.18, 290.55) * mm, "end": v(-778.3, 315.76) * mm});
            skSolve(sketch);
        }
        {
            var Q0;
            Q0 = qSketchRegion(id + "F56", true);
            extrude(context, id + "F57", {"entities" : qUnion([Q0]), "oppositeDirection" : true, "depth" : 3.17 * mm});
        }
        {
            var Q0;
            Q0=makeQuery(id+"F18.opPattern","COPY",FACE,{"derivedFrom":makeQuery(id+"F17.opLoft","SWEPT_FACE",FACE,{"disambiguationData":[OSD([sQuery(id+"F6.wireOp",EDGE,"E8"),sQuery(id+"F10.wireOp",EDGE,"E11"),sQuery(id+"F15.wireOp",EDGE,"E12.bottom"),sQuery(id+"F15.wireOp",EDGE,"E12.left"),sQuery(id+"F15.wireOp",EDGE,"E12.right"),sQuery(id+"F16.wireOp",EDGE,"E13.bottom"),sQuery(id+"F16.wireOp",EDGE,"E13.left"),sQuery(id+"F16.wireOp",EDGE,"E13.right")])]}),"instanceName":"1"});
            var sketch = newSketch(context, id + "F58", { "sketchPlane" : qUnion([Q0])});
            skLineSegment(sketch, "E83", {"start": v(-752.45, 107.31) * mm, "end": v(-714.64, 112) * mm});
            skLineSegment(sketch, "E84", {"start": v(-714.64, 112) * mm, "end": v(-717.77, 137.2) * mm});
            skLineSegment(sketch, "E85", {"start": v(-717.77, 137.2) * mm, "end": v(-755.58, 132.52) * mm});
            skLineSegment(sketch, "E86", {"start": v(-755.58, 132.52) * mm, "end": v(-752.45, 107.31) * mm});
            skSolve(sketch);
        }
        {
            var Q0;
            Q0 = qSketchRegion(id + "F58", true);
            extrude(context, id + "F59", {"entities" : qUnion([Q0]), "oppositeDirection" : true, "depth" : 3.17 * mm});
        }
        {
            var Q0;
            Q0=makeQuery(id+"F19.opPattern","COPY",FACE,{"derivedFrom":makeQuery(id+"F18.opPattern","COPY",FACE,{"derivedFrom":makeQuery(id+"F17.opLoft","SWEPT_FACE",FACE,{"disambiguationData":[OSD([sQuery(id+"F6.wireOp",EDGE,"E8"),sQuery(id+"F10.wireOp",EDGE,"E11"),sQuery(id+"F15.wireOp",EDGE,"E12.bottom"),sQuery(id+"F15.wireOp",EDGE,"E12.left"),sQuery(id+"F15.wireOp",EDGE,"E12.right"),sQuery(id+"F16.wireOp",EDGE,"E13.bottom"),sQuery(id+"F16.wireOp",EDGE,"E13.left"),sQuery(id+"F16.wireOp",EDGE,"E13.right")])]}),"instanceName":"1"}),"instanceName":"1"});
            var sketch = newSketch(context, id + "F60", { "sketchPlane" : qUnion([Q0])});
            skLineSegment(sketch, "E87", {"start": v(752.45, 107.31) * mm, "end": v(714.64, 112) * mm});
            skLineSegment(sketch, "E88", {"start": v(714.64, 112) * mm, "end": v(717.77, 137.2) * mm});
            skLineSegment(sketch, "E89", {"start": v(717.77, 137.2) * mm, "end": v(755.58, 132.52) * mm});
            skLineSegment(sketch, "E90", {"start": v(755.58, 132.52) * mm, "end": v(752.45, 107.31) * mm});
            skSolve(sketch);
        }
        {
            var Q0;
            Q0 = qSketchRegion(id + "F60", true);
            extrude(context, id + "F61", {"entities" : qUnion([Q0]), "oppositeDirection" : true, "depth" : 3.17 * mm});
        }
        {
            var Q0;
            Q0=makeQuery(id+"F19.opPattern","COPY",FACE,{"derivedFrom":makeQuery(id+"F18.opPattern","COPY",FACE,{"derivedFrom":makeQuery(id+"F17.opLoft","SWEPT_FACE",FACE,{"disambiguationData":[OSD([sQuery(id+"F6.wireOp",EDGE,"E8"),sQuery(id+"F10.wireOp",EDGE,"E11"),sQuery(id+"F15.wireOp",EDGE,"E12.bottom"),sQuery(id+"F15.wireOp",EDGE,"E12.left"),sQuery(id+"F15.wireOp",EDGE,"E12.right"),sQuery(id+"F16.wireOp",EDGE,"E13.bottom"),sQuery(id+"F16.wireOp",EDGE,"E13.left"),sQuery(id+"F16.wireOp",EDGE,"E13.right")])]}),"instanceName":"1"}),"instanceName":"1"});
            var sketch = newSketch(context, id + "F62", { "sketchPlane" : qUnion([Q0])});
            skLineSegment(sketch, "E91", {"start": v(803.23, 516.68) * mm, "end": v(765.42, 521.37) * mm});
            skLineSegment(sketch, "E92", {"start": v(765.42, 521.37) * mm, "end": v(762.29, 496.17) * mm});
            skLineSegment(sketch, "E93", {"start": v(762.29, 496.17) * mm, "end": v(800.1, 491.48) * mm});
            skPoint(sketch, "E93.endSnap0", {"position": v(800.1, 491.48) * mm});
            skLineSegment(sketch, "E94", {"start": v(800.1, 491.48) * mm, "end": v(803.23, 516.68) * mm});
            skSolve(sketch);
        }
        {
            var Q0;
            Q0 = qSketchRegion(id + "F62", true);
            extrude(context, id + "F63", {"entities" : qUnion([Q0]), "oppositeDirection" : true, "depth" : 3.17 * mm});
        }
        {
            var Q0;
            Q0=makeQuery(id+"F19.opPattern","COPY",FACE,{"derivedFrom":makeQuery(id+"F18.opPattern","COPY",FACE,{"derivedFrom":makeQuery(id+"F17.opLoft","SWEPT_FACE",FACE,{"disambiguationData":[OSD([sQuery(id+"F6.wireOp",EDGE,"E8"),sQuery(id+"F10.wireOp",EDGE,"E11"),sQuery(id+"F15.wireOp",EDGE,"E12.bottom"),sQuery(id+"F15.wireOp",EDGE,"E12.left"),sQuery(id+"F15.wireOp",EDGE,"E12.right"),sQuery(id+"F16.wireOp",EDGE,"E13.bottom"),sQuery(id+"F16.wireOp",EDGE,"E13.left"),sQuery(id+"F16.wireOp",EDGE,"E13.right")])]}),"instanceName":"1"}),"instanceName":"1"});
            var sketch = newSketch(context, id + "F64", { "sketchPlane" : qUnion([Q0])});
            skLineSegment(sketch, "E95", {"start": v(869.95, 901.04) * mm, "end": v(768.35, 81.91) * mm, "construction": true});
            skSolve(sketch);
        }
        {
            var Q0;
            {var subQ0=sQuery(id+"F15.wireOp",EDGE,"E12.right");var subQ1=sQuery(id+"F15.wireOp",EDGE,"E12.left");var subQ2=sQuery(id+"F15.wireOp",EDGE,"E12.bottom");var subQ3=sQuery(id+"F10.wireOp",EDGE,"E11");Q0=makeQuery(id+"F64.imprint","IMPRINT",FACE,{"disambiguationData":[TD([[makeQuery(id+"F64.imprint","IMPRINT",EDGE,{"derivedFrom":makeQuery(id+"F19.opPattern","COPY",EDGE,{"derivedFrom":makeQuery(id+"F18.opPattern","COPY",EDGE,{"derivedFrom":makeQuery(id+"F17.opLoft","MID_CAP_EDGE",EDGE,{"disambiguationData":[OSD([subQ3,subQ2,subQ1,subQ0])],"capPos":1.0}),"instanceName":"1"}),"instanceName":"1"})}),-1.0]])]});}
            var sketch = newSketch(context, id + "F65", { "sketchPlane" : qUnion([Q0])});
            skLineSegment(sketch, "E96.bottom", {"start": v(877.92, 850.24) * mm, "end": v(852.52, 850.24) * mm});
            skLineSegment(sketch, "E96.top", {"start": v(877.92, 875.64) * mm, "end": v(852.52, 875.64) * mm});
            skLineSegment(sketch, "E96.left", {"start": v(877.92, 850.24) * mm, "end": v(877.92, 875.64) * mm});
            skLineSegment(sketch, "E96.right", {"start": v(852.52, 850.24) * mm, "end": v(852.52, 875.64) * mm});
            skPoint(sketch, "E96.middle", {"position": v(865.22, 862.94) * mm});
            skSolve(sketch);
        }
        {
            var Q0;
            Q0 = qSketchRegion(id + "F65", true);
            extrude(context, id + "F66", {"entities" : qUnion([Q0]), "endBound" : BoundingType.UP_TO_NEXT, "depth" : 25.4 * mm});
        }
        {
            var Q0;
            {var subQ0=sQuery(id+"F15.wireOp",EDGE,"E12.right");var subQ1=sQuery(id+"F15.wireOp",EDGE,"E12.left");var subQ2=sQuery(id+"F15.wireOp",EDGE,"E12.bottom");var subQ3=sQuery(id+"F10.wireOp",EDGE,"E11");Q0=makeQuery(id+"F64.imprint","IMPRINT",FACE,{"disambiguationData":[TD([[makeQuery(id+"F64.imprint","IMPRINT",EDGE,{"derivedFrom":makeQuery(id+"F19.opPattern","COPY",EDGE,{"derivedFrom":makeQuery(id+"F18.opPattern","COPY",EDGE,{"derivedFrom":makeQuery(id+"F17.opLoft","MID_CAP_EDGE",EDGE,{"disambiguationData":[OSD([subQ3,subQ2,subQ1,subQ0])],"capPos":1.0}),"instanceName":"1"}),"instanceName":"1"})}),-1.0]])]});}
            var sketch = newSketch(context, id + "F67", { "sketchPlane" : qUnion([Q0])});
            skLineSegment(sketch, "E97.bottom", {"start": v(850.84, 631.87) * mm, "end": v(825.44, 631.87) * mm});
            skLineSegment(sketch, "E97.top", {"start": v(850.84, 657.27) * mm, "end": v(825.44, 657.27) * mm});
            skLineSegment(sketch, "E97.left", {"start": v(850.84, 631.87) * mm, "end": v(850.84, 657.27) * mm});
            skLineSegment(sketch, "E97.right", {"start": v(825.44, 631.87) * mm, "end": v(825.44, 657.27) * mm});
            skPoint(sketch, "E97.middle", {"position": v(838.14, 644.57) * mm});
            skPoint(sketch, "E98", {"position": v(831.84, 593.77) * mm});
            skSolve(sketch);
        }
        {
            var Q0;
            Q0 = qSketchRegion(id + "F67", true);
            extrude(context, id + "F68", {"entities" : qUnion([Q0]), "endBound" : BoundingType.UP_TO_NEXT, "depth" : 25.4 * mm});
        }
        {
            var Q0;
            Q0=makeQuery(id+"F18.opPattern","COPY",FACE,{"derivedFrom":makeQuery(id+"F17.opLoft","SWEPT_FACE",FACE,{"disambiguationData":[OSD([sQuery(id+"F6.wireOp",EDGE,"E8"),sQuery(id+"F10.wireOp",EDGE,"E11"),sQuery(id+"F15.wireOp",EDGE,"E12.bottom"),sQuery(id+"F15.wireOp",EDGE,"E12.left"),sQuery(id+"F15.wireOp",EDGE,"E12.right"),sQuery(id+"F16.wireOp",EDGE,"E13.bottom"),sQuery(id+"F16.wireOp",EDGE,"E13.left"),sQuery(id+"F16.wireOp",EDGE,"E13.right")])]}),"instanceName":"1"});
            var sketch = newSketch(context, id + "F69", { "sketchPlane" : qUnion([Q0])});
            skLineSegment(sketch, "E99.bottom", {"start": v(-818.19, 568.66) * mm, "end": v(-843.59, 568.66) * mm});
            skLineSegment(sketch, "E99.top", {"start": v(-818.19, 594.06) * mm, "end": v(-843.59, 594.06) * mm});
            skLineSegment(sketch, "E99.left", {"start": v(-818.19, 568.66) * mm, "end": v(-818.19, 594.06) * mm});
            skLineSegment(sketch, "E99.right", {"start": v(-843.59, 568.66) * mm, "end": v(-843.59, 594.06) * mm});
            skPoint(sketch, "E99.middle", {"position": v(-830.89, 581.36) * mm});
            skSolve(sketch);
        }
        {
            var Q0;
            Q0 = qSketchRegion(id + "F69", true);
            extrude(context, id + "F70", {"entities" : qUnion([Q0]), "endBound" : BoundingType.UP_TO_NEXT, "depth" : 25.4 * mm});
        }
        {
            var Q0;
            Q0=makeQuery(id+"F18.opPattern","COPY",FACE,{"derivedFrom":makeQuery(id+"F17.opLoft","SWEPT_FACE",FACE,{"disambiguationData":[OSD([sQuery(id+"F6.wireOp",EDGE,"E8"),sQuery(id+"F10.wireOp",EDGE,"E11"),sQuery(id+"F15.wireOp",EDGE,"E12.bottom"),sQuery(id+"F15.wireOp",EDGE,"E12.left"),sQuery(id+"F15.wireOp",EDGE,"E12.right"),sQuery(id+"F16.wireOp",EDGE,"E13.bottom"),sQuery(id+"F16.wireOp",EDGE,"E13.left"),sQuery(id+"F16.wireOp",EDGE,"E13.right")])]}),"instanceName":"1"});
            var sketch = newSketch(context, id + "F71", { "sketchPlane" : qUnion([Q0])});
            skLineSegment(sketch, "E100.bottom", {"start": v(-792, 357.52) * mm, "end": v(-817.4, 357.52) * mm});
            skLineSegment(sketch, "E100.top", {"start": v(-792, 382.92) * mm, "end": v(-817.4, 382.92) * mm});
            skLineSegment(sketch, "E100.left", {"start": v(-792, 357.52) * mm, "end": v(-792, 382.92) * mm});
            skLineSegment(sketch, "E100.right", {"start": v(-817.4, 357.52) * mm, "end": v(-817.4, 382.92) * mm});
            skPoint(sketch, "E100.middle", {"position": v(-804.7, 370.22) * mm});
            skPoint(sketch, "E101", {"position": v(-796.82, 306.72) * mm});
            skSolve(sketch);
        }
        {
            var Q0;
            Q0 = qSketchRegion(id + "F71", true);
            extrude(context, id + "F72", {"entities" : qUnion([Q0]), "endBound" : BoundingType.UP_TO_NEXT, "depth" : 25.4 * mm});
        }
        {
            var Q0;
            Q0=makeQuery(id+"F18.opPattern","COPY",FACE,{"derivedFrom":makeQuery(id+"F17.opLoft","SWEPT_FACE",FACE,{"disambiguationData":[OSD([sQuery(id+"F6.wireOp",EDGE,"E6"),sQuery(id+"F10.wireOp",EDGE,"E9"),sQuery(id+"F15.wireOp",EDGE,"E12.bottom"),sQuery(id+"F15.wireOp",EDGE,"E12.top"),sQuery(id+"F15.wireOp",EDGE,"E12.left"),sQuery(id+"F16.wireOp",EDGE,"E13.bottom"),sQuery(id+"F16.wireOp",EDGE,"E13.top"),sQuery(id+"F16.wireOp",EDGE,"E13.left")])]}),"instanceName":"1"});
            var sketch = newSketch(context, id + "F73", { "sketchPlane" : qUnion([Q0])});
            skLineSegment(sketch, "E102.bottom", {"start": v(310.19, 634.82) * mm, "end": v(284.79, 634.82) * mm});
            skLineSegment(sketch, "E102.top", {"start": v(310.19, 660.22) * mm, "end": v(284.79, 660.22) * mm});
            skLineSegment(sketch, "E102.left", {"start": v(310.19, 634.82) * mm, "end": v(310.19, 660.22) * mm});
            skLineSegment(sketch, "E102.right", {"start": v(284.79, 634.82) * mm, "end": v(284.79, 660.22) * mm});
            skPoint(sketch, "E102.middle", {"position": v(297.49, 647.52) * mm});
            skSolve(sketch);
        }
        {
            var Q0;
            Q0 = qSketchRegion(id + "F73", true);
            extrude(context, id + "F74", {"entities" : qUnion([Q0]), "endBound" : BoundingType.UP_TO_NEXT, "depth" : 25.4 * mm});
        }
        {
            var Q0;
            Q0=makeQuery(id+"F18.opPattern","COPY",FACE,{"derivedFrom":makeQuery(id+"F17.opLoft","SWEPT_FACE",FACE,{"disambiguationData":[OSD([sQuery(id+"F6.wireOp",EDGE,"E6"),sQuery(id+"F10.wireOp",EDGE,"E9"),sQuery(id+"F15.wireOp",EDGE,"E12.bottom"),sQuery(id+"F15.wireOp",EDGE,"E12.top"),sQuery(id+"F15.wireOp",EDGE,"E12.left"),sQuery(id+"F16.wireOp",EDGE,"E13.bottom"),sQuery(id+"F16.wireOp",EDGE,"E13.top"),sQuery(id+"F16.wireOp",EDGE,"E13.left")])]}),"instanceName":"1"});
            var sketch = newSketch(context, id + "F75", { "sketchPlane" : qUnion([Q0])});
            skLineSegment(sketch, "E103.bottom", {"start": v(283.69, 421.19) * mm, "end": v(258.29, 421.19) * mm});
            skLineSegment(sketch, "E103.top", {"start": v(283.69, 446.59) * mm, "end": v(258.29, 446.59) * mm});
            skLineSegment(sketch, "E103.left", {"start": v(283.69, 421.19) * mm, "end": v(283.69, 446.59) * mm});
            skLineSegment(sketch, "E103.right", {"start": v(258.29, 421.19) * mm, "end": v(258.29, 446.59) * mm});
            skPoint(sketch, "E103.middle", {"position": v(270.99, 433.89) * mm});
            skPoint(sketch, "E104", {"position": v(264.69, 383.09) * mm});
            skSolve(sketch);
        }
        {
            var Q0;
            Q0 = qSketchRegion(id + "F75", true);
            extrude(context, id + "F76", {"entities" : qUnion([Q0]), "endBound" : BoundingType.UP_TO_NEXT, "depth" : 25.4 * mm});
        }
        {
            var Q0;
            Q0=makeQuery(id+"F17.opLoft","SWEPT_FACE",FACE,{"disambiguationData":[OSD([sQuery(id+"F6.wireOp",EDGE,"E6"),sQuery(id+"F10.wireOp",EDGE,"E9"),sQuery(id+"F15.wireOp",EDGE,"E12.bottom"),sQuery(id+"F15.wireOp",EDGE,"E12.top"),sQuery(id+"F15.wireOp",EDGE,"E12.left"),sQuery(id+"F16.wireOp",EDGE,"E13.bottom"),sQuery(id+"F16.wireOp",EDGE,"E13.top"),sQuery(id+"F16.wireOp",EDGE,"E13.left")])]});
            var sketch = newSketch(context, id + "F77", { "sketchPlane" : qUnion([Q0])});
            skLineSegment(sketch, "E105", {"start": v(-336.55, 967.2) * mm, "end": v(-234.95, 148.07) * mm, "construction": true});
            skSolve(sketch);
        }
        {
            var Q0;
            {var subQ0=sQuery(id+"F15.wireOp",EDGE,"E12.left");var subQ1=sQuery(id+"F15.wireOp",EDGE,"E12.top");var subQ2=sQuery(id+"F15.wireOp",EDGE,"E12.bottom");var subQ3=sQuery(id+"F10.wireOp",EDGE,"E9");Q0=makeQuery(id+"F77.imprint","IMPRINT",FACE,{"disambiguationData":[TD([[makeQuery(id+"F77.imprint","IMPRINT",EDGE,{"derivedFrom":makeQuery(id+"F17.opLoft","MID_CAP_EDGE",EDGE,{"disambiguationData":[OSD([subQ3,subQ2,subQ1,subQ0])],"capPos":1.0})}),-1.0]])]});}
            var sketch = newSketch(context, id + "F78", { "sketchPlane" : qUnion([Q0])});
            skLineSegment(sketch, "E106.bottom", {"start": v(-319.52, 919.55) * mm, "end": v(-344.92, 919.55) * mm});
            skLineSegment(sketch, "E106.top", {"start": v(-319.52, 944.95) * mm, "end": v(-344.92, 944.95) * mm});
            skLineSegment(sketch, "E106.left", {"start": v(-319.52, 919.55) * mm, "end": v(-319.52, 944.95) * mm});
            skLineSegment(sketch, "E106.right", {"start": v(-344.92, 919.55) * mm, "end": v(-344.92, 944.95) * mm});
            skPoint(sketch, "E106.middle", {"position": v(-332.22, 932.25) * mm});
            skSolve(sketch);
        }
        {
            var Q0;
            Q0 = qSketchRegion(id + "F78", true);
            extrude(context, id + "F79", {"entities" : qUnion([Q0]), "endBound" : BoundingType.UP_TO_NEXT, "depth" : 25.4 * mm});
        }
        {
            var Q0;
            {var subQ0=sQuery(id+"F15.wireOp",EDGE,"E12.left");var subQ1=sQuery(id+"F15.wireOp",EDGE,"E12.top");var subQ2=sQuery(id+"F15.wireOp",EDGE,"E12.bottom");var subQ3=sQuery(id+"F10.wireOp",EDGE,"E9");Q0=makeQuery(id+"F77.imprint","IMPRINT",FACE,{"disambiguationData":[TD([[makeQuery(id+"F77.imprint","IMPRINT",EDGE,{"derivedFrom":makeQuery(id+"F17.opLoft","MID_CAP_EDGE",EDGE,{"disambiguationData":[OSD([subQ3,subQ2,subQ1,subQ0])],"capPos":1.0})}),-1.0]])]});}
            var sketch = newSketch(context, id + "F80", { "sketchPlane" : qUnion([Q0])});
            skLineSegment(sketch, "E107.bottom", {"start": v(-289.05, 696.76) * mm, "end": v(-314.45, 696.76) * mm});
            skLineSegment(sketch, "E107.top", {"start": v(-289.05, 722.16) * mm, "end": v(-314.45, 722.16) * mm});
            skLineSegment(sketch, "E107.left", {"start": v(-289.05, 696.76) * mm, "end": v(-289.05, 722.16) * mm});
            skLineSegment(sketch, "E107.right", {"start": v(-314.45, 696.76) * mm, "end": v(-314.45, 722.16) * mm});
            skPoint(sketch, "E107.middle", {"position": v(-301.75, 709.46) * mm});
            skPoint(sketch, "E108", {"position": v(-296.7, 645.96) * mm});
            skSolve(sketch);
        }
        {
            var Q0;
            Q0 = qSketchRegion(id + "F80", true);
            extrude(context, id + "F81", {"entities" : qUnion([Q0]), "endBound" : BoundingType.UP_TO_NEXT, "depth" : 25.4 * mm});
        }
        {
            var Q0;
            Q0=makeQuery(id+"F19.opPattern","COPY",FACE,{"derivedFrom":makeQuery(id+"F17.opLoft","SWEPT_FACE",FACE,{"disambiguationData":[OSD([sQuery(id+"F6.wireOp",EDGE,"E6"),sQuery(id+"F10.wireOp",EDGE,"E9"),sQuery(id+"F15.wireOp",EDGE,"E12.bottom"),sQuery(id+"F15.wireOp",EDGE,"E12.top"),sQuery(id+"F15.wireOp",EDGE,"E12.left"),sQuery(id+"F16.wireOp",EDGE,"E13.bottom"),sQuery(id+"F16.wireOp",EDGE,"E13.top"),sQuery(id+"F16.wireOp",EDGE,"E13.left")])]}),"instanceName":"1"});
            var sketch = newSketch(context, id + "F82", { "sketchPlane" : qUnion([Q0])});
            skLineSegment(sketch, "E109", {"start": v(336.55, 967.2) * mm, "end": v(234.95, 148.07) * mm, "construction": true});
            skLineSegment(sketch, "E110.MirrorCS", {"start": v(-336.55, 967.2) * mm, "end": v(-234.95, 148.07) * mm, "construction": true});
            skSolve(sketch);
        }
        {
            var Q0;
            {var subQ0=sQuery(id+"F15.wireOp",EDGE,"E12.left");var subQ1=sQuery(id+"F15.wireOp",EDGE,"E12.top");var subQ2=sQuery(id+"F15.wireOp",EDGE,"E12.bottom");var subQ3=sQuery(id+"F10.wireOp",EDGE,"E9");Q0=makeQuery(id+"F82.imprint","IMPRINT",FACE,{"disambiguationData":[TD([[makeQuery(id+"F82.imprint","IMPRINT",EDGE,{"derivedFrom":makeQuery(id+"F19.opPattern","COPY",EDGE,{"derivedFrom":makeQuery(id+"F17.opLoft","MID_CAP_EDGE",EDGE,{"disambiguationData":[OSD([subQ3,subQ2,subQ1,subQ0])],"capPos":1.0}),"instanceName":"1"})}),1.0]])]});}
            var sketch = newSketch(context, id + "F83", { "sketchPlane" : qUnion([Q0])});
            skLineSegment(sketch, "E111.bottom", {"start": v(344.52, 916.4) * mm, "end": v(319.12, 916.4) * mm});
            skLineSegment(sketch, "E111.top", {"start": v(344.52, 941.8) * mm, "end": v(319.12, 941.8) * mm});
            skLineSegment(sketch, "E111.left", {"start": v(344.52, 916.4) * mm, "end": v(344.52, 941.8) * mm});
            skLineSegment(sketch, "E111.right", {"start": v(319.12, 916.4) * mm, "end": v(319.12, 941.8) * mm});
            skPoint(sketch, "E111.middle", {"position": v(331.82, 929.1) * mm});
            skSolve(sketch);
        }
        {
            var Q0;
            Q0 = qSketchRegion(id + "F83", true);
            extrude(context, id + "F84", {"entities" : qUnion([Q0]), "endBound" : BoundingType.UP_TO_NEXT, "depth" : 25.4 * mm});
        }
        {
            var Q0;
            {var subQ0=sQuery(id+"F15.wireOp",EDGE,"E12.left");var subQ1=sQuery(id+"F15.wireOp",EDGE,"E12.top");var subQ2=sQuery(id+"F15.wireOp",EDGE,"E12.bottom");var subQ3=sQuery(id+"F10.wireOp",EDGE,"E9");Q0=makeQuery(id+"F82.imprint","IMPRINT",FACE,{"disambiguationData":[TD([[makeQuery(id+"F82.imprint","IMPRINT",EDGE,{"derivedFrom":makeQuery(id+"F19.opPattern","COPY",EDGE,{"derivedFrom":makeQuery(id+"F17.opLoft","MID_CAP_EDGE",EDGE,{"disambiguationData":[OSD([subQ3,subQ2,subQ1,subQ0])],"capPos":1.0}),"instanceName":"1"})}),1.0]])]});}
            var sketch = newSketch(context, id + "F85", { "sketchPlane" : qUnion([Q0])});
            skLineSegment(sketch, "E112.bottom", {"start": v(325.85, 765.86) * mm, "end": v(300.45, 765.86) * mm});
            skLineSegment(sketch, "E112.top", {"start": v(325.85, 791.26) * mm, "end": v(300.45, 791.26) * mm});
            skLineSegment(sketch, "E112.left", {"start": v(325.85, 765.86) * mm, "end": v(325.85, 791.26) * mm});
            skLineSegment(sketch, "E112.right", {"start": v(300.45, 765.86) * mm, "end": v(300.45, 791.26) * mm});
            skPoint(sketch, "E112.middle", {"position": v(313.15, 778.56) * mm});
            skPoint(sketch, "E113", {"position": v(305.28, 715.06) * mm});
            skSolve(sketch);
        }
        {
            var Q0;
            Q0 = qSketchRegion(id + "F85", true);
            extrude(context, id + "F86", {"entities" : qUnion([Q0]), "endBound" : BoundingType.UP_TO_NEXT, "depth" : 25.4 * mm});
        }
        {
            var Q0;
            Q0=makeQuery(id+"F19.opPattern","COPY",FACE,{"derivedFrom":makeQuery(id+"F18.opPattern","COPY",FACE,{"derivedFrom":makeQuery(id+"F17.opLoft","SWEPT_FACE",FACE,{"disambiguationData":[OSD([sQuery(id+"F6.wireOp",EDGE,"E6"),sQuery(id+"F10.wireOp",EDGE,"E9"),sQuery(id+"F15.wireOp",EDGE,"E12.bottom"),sQuery(id+"F15.wireOp",EDGE,"E12.top"),sQuery(id+"F15.wireOp",EDGE,"E12.left"),sQuery(id+"F16.wireOp",EDGE,"E13.bottom"),sQuery(id+"F16.wireOp",EDGE,"E13.top"),sQuery(id+"F16.wireOp",EDGE,"E13.left")])]}),"instanceName":"1"}),"instanceName":"1"});
            var sketch = newSketch(context, id + "F87", { "sketchPlane" : qUnion([Q0])});
            skLineSegment(sketch, "E114.bottom", {"start": v(-319.12, 916.4) * mm, "end": v(-344.52, 916.4) * mm});
            skLineSegment(sketch, "E114.top", {"start": v(-319.12, 941.8) * mm, "end": v(-344.52, 941.8) * mm});
            skLineSegment(sketch, "E114.left", {"start": v(-319.12, 916.4) * mm, "end": v(-319.12, 941.8) * mm});
            skLineSegment(sketch, "E114.right", {"start": v(-344.52, 916.4) * mm, "end": v(-344.52, 941.8) * mm});
            skPoint(sketch, "E114.middle", {"position": v(-331.82, 929.1) * mm});
            skSolve(sketch);
        }
        {
            var Q0;
            Q0 = qSketchRegion(id + "F87", true);
            extrude(context, id + "F88", {"entities" : qUnion([Q0]), "endBound" : BoundingType.UP_TO_NEXT, "depth" : 25.4 * mm});
        }
        {
            var Q0;
            Q0=makeQuery(id+"F19.opPattern","COPY",FACE,{"derivedFrom":makeQuery(id+"F18.opPattern","COPY",FACE,{"derivedFrom":makeQuery(id+"F17.opLoft","SWEPT_FACE",FACE,{"disambiguationData":[OSD([sQuery(id+"F6.wireOp",EDGE,"E6"),sQuery(id+"F10.wireOp",EDGE,"E9"),sQuery(id+"F15.wireOp",EDGE,"E12.bottom"),sQuery(id+"F15.wireOp",EDGE,"E12.top"),sQuery(id+"F15.wireOp",EDGE,"E12.left"),sQuery(id+"F16.wireOp",EDGE,"E13.bottom"),sQuery(id+"F16.wireOp",EDGE,"E13.top"),sQuery(id+"F16.wireOp",EDGE,"E13.left")])]}),"instanceName":"1"}),"instanceName":"1"});
            var sketch = newSketch(context, id + "F89", { "sketchPlane" : qUnion([Q0])});
            skLineSegment(sketch, "E115.bottom", {"start": v(-295.02, 722.07) * mm, "end": v(-320.42, 722.07) * mm});
            skLineSegment(sketch, "E115.top", {"start": v(-295.02, 747.47) * mm, "end": v(-320.42, 747.47) * mm});
            skLineSegment(sketch, "E115.left", {"start": v(-295.02, 722.07) * mm, "end": v(-295.02, 747.47) * mm});
            skLineSegment(sketch, "E115.right", {"start": v(-320.42, 722.07) * mm, "end": v(-320.42, 747.47) * mm});
            skPoint(sketch, "E115.middle", {"position": v(-307.72, 734.77) * mm});
            skPoint(sketch, "E116", {"position": v(-299.84, 671.27) * mm});
            skSolve(sketch);
        }
        {
            var Q0;
            Q0 = qSketchRegion(id + "F89", true);
            extrude(context, id + "F90", {"entities" : qUnion([Q0]), "endBound" : BoundingType.UP_TO_NEXT, "depth" : 25.4 * mm});
        }
        {
            var Q0;
            Q0=qCreatedBy(makeId("Right.planeOp"),FACE);
            var sketch = newSketch(context, id + "F91", { "sketchPlane" : qUnion([Q0])});
            skLineSegment(sketch, "E117.bottom", {"start": v(276.22, 533.4) * mm, "end": v(250.82, 533.4) * mm});
            skLineSegment(sketch, "E117.top", {"start": v(276.22, 584.2) * mm, "end": v(250.82, 584.2) * mm});
            skLineSegment(sketch, "E117.left", {"start": v(276.22, 533.4) * mm, "end": v(276.22, 584.2) * mm});
            skLineSegment(sketch, "E117.right", {"start": v(250.82, 533.4) * mm, "end": v(250.82, 584.2) * mm});
            skSolve(sketch);
        }
        {
            var Q0;
            Q0 = qSketchRegion(id + "F91", true);
            extrude(context, id + "F92", {"entities" : qUnion([Q0]), "endBound" : BoundingType.UP_TO_NEXT, "depth" : 25.4 * mm, "hasSecondDirection" : true, "secondDirectionBound" : SecondDirectionBoundingType.UP_TO_NEXT, "secondDirectionOppositeDirection" : true, "secondDirectionDepth" : 25.4 * mm});
        }
        {
            var Q0;
            Q0=makeQuery(id+"F92.opExtrude","SWEPT_FACE",FACE,{"disambiguationData":[OSD([sQuery(id+"F91.wireOp",EDGE,"E117.left")])]});
            var sketch = newSketch(context, id + "F93", { "sketchPlane" : qUnion([Q0])});
            skLineSegment(sketch, "E118", {"start": v(874.68, 584.2) * mm, "end": v(-815.98, 584.2) * mm});
            skLineSegment(sketch, "E119", {"start": v(-815.98, 584.2) * mm, "end": v(-815.98, 587.38) * mm});
            skLineSegment(sketch, "E120", {"start": v(-815.98, 587.38) * mm, "end": v(875.07, 587.38) * mm});
            skLineSegment(sketch, "E121", {"start": v(875.07, 587.38) * mm, "end": v(874.68, 584.2) * mm});
            skSolve(sketch);
        }
        {
            var Q0;
            Q0 = qSketchRegion(id + "F93", true);
            var Q1;
            Q1=makeQuery(id+"F22.opExtrude","CAP_FACE",FACE,{"disambiguationData":[OSD([sQuery(id+"F21.wireOp",EDGE,"E14"),sQuery(id+"F21.wireOp",EDGE,"E15"),sQuery(id+"F21.wireOp",EDGE,"E16"),sQuery(id+"F21.wireOp",EDGE,"E17"),sQuery(id+"F21.wireOp",EDGE,"E18"),sQuery(id+"F21.wireOp",EDGE,"E19")])],"isStart":false});
            extrude(context, id + "F94", {"entities" : qUnion([Q0]), "endBound" : BoundingType.UP_TO_SURFACE, "oppositeDirection" : true, "endBoundEntityFace" : qUnion([Q1]), "depth" : 25.4 * mm});
        }
        {
            var Q0;
            Q0=makeQuery(id+"F92.opExtrude","SWEPT_FACE",FACE,{"disambiguationData":[OSD([sQuery(id+"F91.wireOp",EDGE,"E117.left")])]});
            var sketch = newSketch(context, id + "F95", { "sketchPlane" : qUnion([Q0])});
            skLineSegment(sketch, "E122", {"start": v(-721.42, 587.38) * mm, "end": v(-822.74, 863.6) * mm});
            skLineSegment(sketch, "E123", {"start": v(-822.74, 863.6) * mm, "end": v(-826.12, 863.6) * mm});
            skLineSegment(sketch, "E124", {"start": v(-826.12, 863.6) * mm, "end": v(-724.8, 587.38) * mm});
            skLineSegment(sketch, "E125", {"start": v(-724.8, 587.38) * mm, "end": v(-721.42, 587.38) * mm});
            skSolve(sketch);
        }
        {
            var Q0;
            Q0 = qSketchRegion(id + "F95", true);
            var Q1;
            Q1=makeQuery(id+"F22.opExtrude","CAP_FACE",FACE,{"disambiguationData":[OSD([sQuery(id+"F21.wireOp",EDGE,"E14"),sQuery(id+"F21.wireOp",EDGE,"E15"),sQuery(id+"F21.wireOp",EDGE,"E16"),sQuery(id+"F21.wireOp",EDGE,"E17"),sQuery(id+"F21.wireOp",EDGE,"E18"),sQuery(id+"F21.wireOp",EDGE,"E19")])],"isStart":false});
            extrude(context, id + "F96", {"entities" : qUnion([Q0]), "endBound" : BoundingType.UP_TO_SURFACE, "oppositeDirection" : true, "endBoundEntityFace" : qUnion([Q1]), "depth" : 25.4 * mm});
        }
        {
            var Q0;
            Q0=makeQuery(id+"F22.opExtrude","CAP_FACE",FACE,{"disambiguationData":[OSD([sQuery(id+"F21.wireOp",EDGE,"E14"),sQuery(id+"F21.wireOp",EDGE,"E15"),sQuery(id+"F21.wireOp",EDGE,"E16"),sQuery(id+"F21.wireOp",EDGE,"E17"),sQuery(id+"F21.wireOp",EDGE,"E18"),sQuery(id+"F21.wireOp",EDGE,"E19")])],"isStart":true});
            var sketch = newSketch(context, id + "F97", { "sketchPlane" : qUnion([Q0])});
            skLineSegment(sketch, "E126", {"start": v(-857.5, 650.19) * mm, "end": v(-854.08, 622.61) * mm});
            skLineSegment(sketch, "E127", {"start": v(-854.08, 622.61) * mm, "end": v(-815.98, 622.61) * mm});
            skLineSegment(sketch, "E128", {"start": v(-815.98, 622.61) * mm, "end": v(-819.4, 650.19) * mm});
            skLineSegment(sketch, "E129", {"start": v(-819.4, 650.19) * mm, "end": v(-857.5, 650.19) * mm});
            skSolve(sketch);
        }
        {
            var Q0;
            Q0 = qSketchRegion(id + "F97", true);
            extrude(context, id + "F98", {"entities" : qUnion([Q0]), "operationType" : NewBodyOperationType.ADD, "oppositeDirection" : true, "depth" : 3 / 406.4 * mm});
        }
        {
            var Q0;
            Q0=makeQuery(id+"F2.opExtrude","SWEPT_BODY",BODY,{"disambiguationData":[OSD([sQuery(id+"F1.wireOp",EDGE,"E0.bottom"),sQuery(id+"F1.wireOp",EDGE,"E0.top"),sQuery(id+"F1.wireOp",EDGE,"E0.left"),sQuery(id+"F1.wireOp",EDGE,"E0.right"),sQuery(id+"F1.wireOp",EDGE,"E1.0"),sQuery(id+"F1.wireOp",EDGE,"E1.1"),sQuery(id+"F1.wireOp",EDGE,"E1.2"),sQuery(id+"F1.wireOp",EDGE,"E1.3")])]});
            transform(context, id + "F99", {"entities" : qUnion([Q0]), "transformType" : TransformType.TRANSLATION_3D, "dx" : 0 * mm, "dy" : 0 * mm, "dz" : 0 * mm, "makeCopy" : true});
        }
    });
